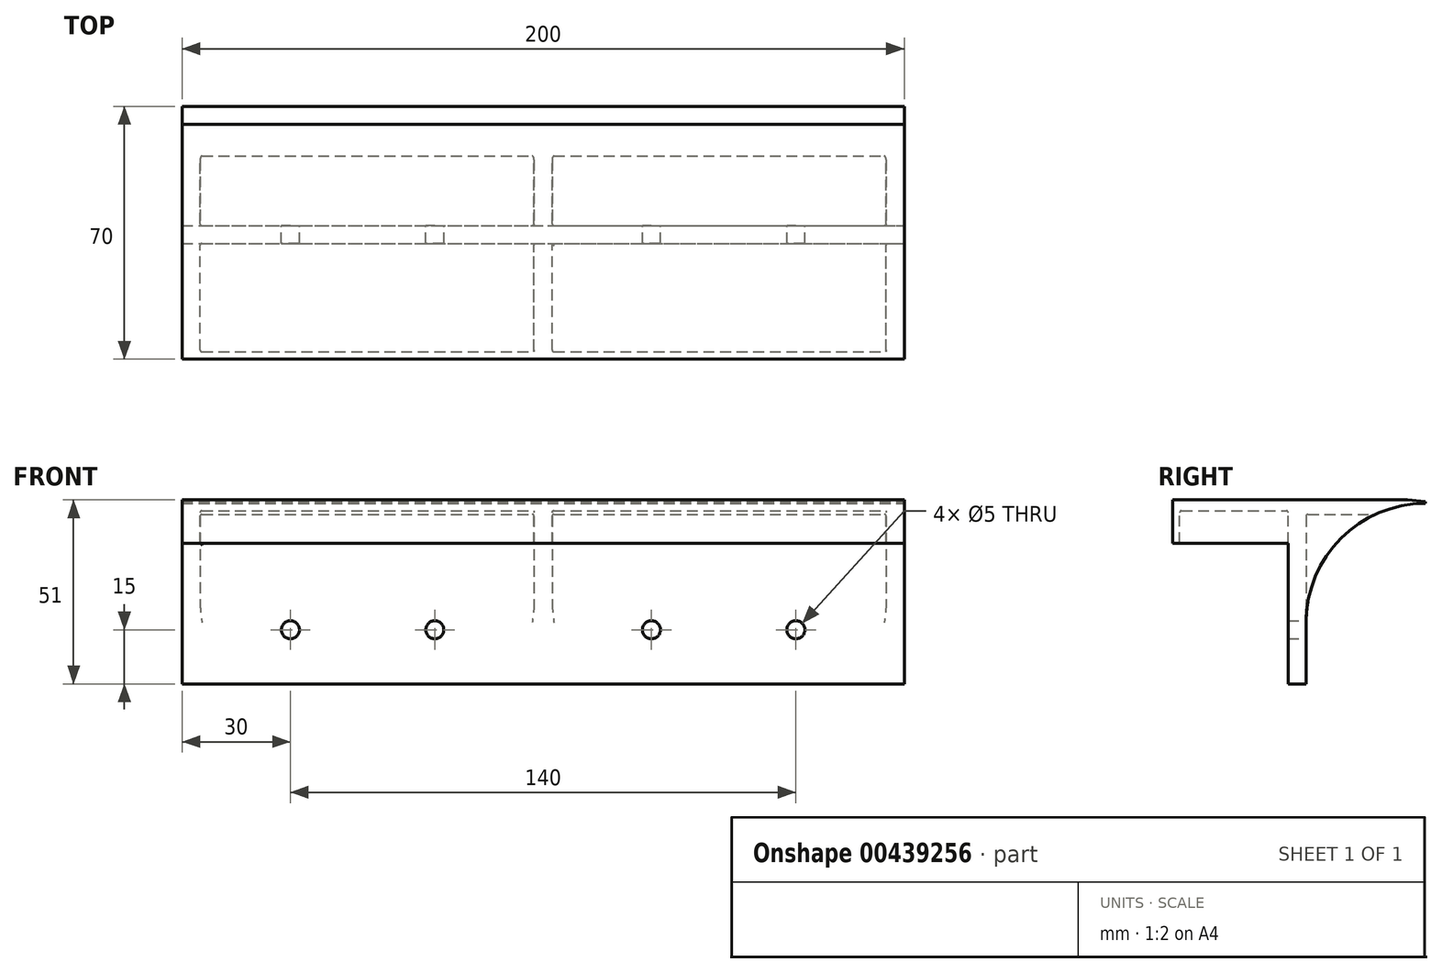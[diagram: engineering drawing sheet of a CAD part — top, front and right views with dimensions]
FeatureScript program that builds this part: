
annotation { "Feature Type Name" : "Feature", "Feature Type Description" : "" }
export const myFeature = defineFeature(function(context is Context, id is Id, definition is map)
    precondition{}
    {
        {
            var Q0;
            Q0=qCreatedBy(makeId("Front.planeOp"),FACE);
            var sketch = newSketch(context, id + "F0", { "sketchPlane" : qUnion([Q0])});
            skLineSegment(sketch, "E0.bottom", {"start": v(0, 0) * mm, "end": v(-200, 0) * mm});
            skLineSegment(sketch, "E0.top", {"start": v(0, -50) * mm, "end": v(-200, -50) * mm});
            skLineSegment(sketch, "E0.left", {"start": v(0, 0) * mm, "end": v(0, -50) * mm});
            skLineSegment(sketch, "E0.right", {"start": v(-200, 0) * mm, "end": v(-200, -50) * mm});
            skLineSegment(sketch, "E1.top", {"start": v(0, 1) * mm, "end": v(-200, 1) * mm});
            skLineSegment(sketch, "E1.left", {"start": v(0, 0) * mm, "end": v(0, 1) * mm});
            skLineSegment(sketch, "E1.right", {"start": v(-200, 0) * mm, "end": v(-200, 1) * mm});
            skSolve(sketch);
        }
        {
            var Q0;
            Q0 = qSketchRegion(id + "F0", true);
            extrude(context, id + "F1", {"entities" : qUnion([Q0]), "depth" : 70 * mm});
        }
        {
            var Q0;
            Q0=qCreatedBy(makeId("Right.planeOp"),FACE);
            var sketch = newSketch(context, id + "F2", { "sketchPlane" : qUnion([Q0])});
            skLineSegment(sketch, "E2.right", {"start": v(-70, -11) * mm, "end": v(-70, -50) * mm});
            skLineSegment(sketch, "E3.top", {"start": v(-70, -11) * mm, "end": v(-38, -11) * mm});
            skLineSegment(sketch, "E3.left", {"start": v(-70, -50) * mm, "end": v(-70, -11) * mm});
            skLineSegment(sketch, "E3.right", {"start": v(-38, -50) * mm, "end": v(-38, -11) * mm});
            skLineSegment(sketch, "E4", {"start": v(-70, -50) * mm, "end": v(-38, -50) * mm});
            skSolve(sketch);
        }
        {
            var Q0;
            Q0 = qSketchRegion(id + "F2", true);
            extrude(context, id + "F3", {"entities" : qUnion([Q0]), "operationType" : NewBodyOperationType.REMOVE, "oppositeDirection" : true, "depth" : 200 * mm});
        }
        {
            var Q0;
            Q0=qCreatedBy(makeId("Right.planeOp"),FACE);
            var sketch = newSketch(context, id + "F4", { "sketchPlane" : qUnion([Q0])});
            skArc(sketch, "E5", {"start": v(0, 0) * mm, "mid": v(-23.33, -9.67) * mm, "end": v(-33, -33) * mm});
            skLineSegment(sketch, "E6", {"start": v(-33, -33) * mm, "end": v(-33, -50) * mm});
            skLineSegment(sketch, "E7", {"start": v(-33, -50) * mm, "end": v(0, -50) * mm});
            skLineSegment(sketch, "E8", {"start": v(0, -50) * mm, "end": v(0, 0) * mm});
            skSolve(sketch);
        }
        {
            var Q0;
            Q0 = qSketchRegion(id + "F4", true);
            extrude(context, id + "F5", {"entities" : qUnion([Q0]), "operationType" : NewBodyOperationType.REMOVE, "oppositeDirection" : true, "depth" : 200 * mm});
        }
        {
            var Q0;
            Q0=qCreatedBy(makeId("Right.planeOp"),FACE);
            var sketch = newSketch(context, id + "F6", { "sketchPlane" : qUnion([Q0])});
            skLineSegment(sketch, "E9.bottom", {"start": v(-68, -11) * mm, "end": v(-38, -11) * mm});
            skLineSegment(sketch, "E9.top", {"start": v(-68, -2) * mm, "end": v(-38, -2) * mm});
            skLineSegment(sketch, "E9.left", {"start": v(-68, -11) * mm, "end": v(-68, -2) * mm});
            skLineSegment(sketch, "E9.right", {"start": v(-38, -11) * mm, "end": v(-38, -2) * mm});
            skSolve(sketch);
        }
        {
            var Q0;
            Q0 = qSketchRegion(id + "F6", true);
            extrude(context, id + "F7", {"entities" : qUnion([Q0]), "operationType" : NewBodyOperationType.REMOVE, "oppositeDirection" : true, "depth" : 195 * mm});
        }
        {
            var Q0;
            Q0 = qSketchRegion(id + "F6", true);
            extrude(context, id + "F8", {"entities" : qUnion([Q0]), "operationType" : NewBodyOperationType.ADD, "oppositeDirection" : true, "depth" : 5 * mm});
        }
        {
            var Q0;
            Q0 = qSketchRegion(id + "F6", true);
            extrude(context, id + "F9", {"entities" : qUnion([Q0]), "operationType" : NewBodyOperationType.ADD, "oppositeDirection" : true, "depth" : 102.5 * mm, "hasSecondDirection" : true, "secondDirectionOppositeDirection" : true, "secondDirectionDepth" : 97.5 * mm});
        }
        {
            var Q0;
            Q0=qCreatedBy(makeId("Right.planeOp"),FACE);
            var sketch = newSketch(context, id + "F10", { "sketchPlane" : qUnion([Q0])});
            skLineSegment(sketch, "E10.bottom", {"start": v(-33, -3) * mm, "end": v(-4.94, -3) * mm});
            skLineSegment(sketch, "E10.top", {"start": v(-33, -33) * mm, "end": v(-4.94, -33) * mm});
            skLineSegment(sketch, "E10.left", {"start": v(-33, -3) * mm, "end": v(-33, -33) * mm});
            skLineSegment(sketch, "E10.right", {"start": v(-4.94, -3) * mm, "end": v(-4.94, -33) * mm});
            skSolve(sketch);
        }
        {
            var Q0;
            Q0 = qSketchRegion(id + "F10", true);
            extrude(context, id + "F11", {"entities" : qUnion([Q0]), "operationType" : NewBodyOperationType.REMOVE, "oppositeDirection" : true, "depth" : 97.5 * mm, "hasSecondDirection" : true, "secondDirectionOppositeDirection" : true, "secondDirectionDepth" : 5 * mm});
        }
        {
            var Q0;
            Q0 = qSketchRegion(id + "F10", true);
            extrude(context, id + "F12", {"entities" : qUnion([Q0]), "operationType" : NewBodyOperationType.REMOVE, "oppositeDirection" : true, "depth" : 195 * mm, "hasSecondDirection" : true, "secondDirectionOppositeDirection" : true, "secondDirectionDepth" : 102.5 * mm});
        }
        {
            var Q0;
            Q0=qCreatedBy(makeId("Front.planeOp"),FACE);
            var sketch = newSketch(context, id + "F13", { "sketchPlane" : qUnion([Q0])});
            skCircle(sketch, "E11", {"center": v(-30, -35) * mm, "radius": 2.5 * mm});
            skCircle(sketch, "E12", {"center": v(-70, -35) * mm, "radius": 2.5 * mm});
            skCircle(sketch, "E13", {"center": v(-130, -35) * mm, "radius": 2.5 * mm});
            skCircle(sketch, "E14", {"center": v(-170, -35) * mm, "radius": 2.5 * mm});
            skSolve(sketch);
        }
        {
            var Q0;
            Q0 = qSketchRegion(id + "F13", true);
            extrude(context, id + "F14", {"entities" : qUnion([Q0]), "operationType" : NewBodyOperationType.REMOVE, "depth" : 60 * mm});
        }
        {
            var Q0;
            Q0=makeQuery(id+"F12.boolean.opBoolean","COPY",EDGE,{"derivedFrom":makeQuery(id+"F12.opExtrude","CAP_EDGE",EDGE,{"disambiguationData":[OSD([sQuery(id+"F10.wireOp",EDGE,"E10.bottom")])],"isStart":false})});
            var Q1;
            Q1=makeQuery(id+"F12.boolean.opBoolean","COPY",EDGE,{"derivedFrom":makeQuery(id+"F12.opExtrude","SWEPT_EDGE",EDGE,{"disambiguationData":[OSD([sQuery(id+"F10.wireOp",EDGE,"E10.bottom"),sQuery(id+"F10.wireOp",EDGE,"E10.left")])]})});
            var Q2;
            Q2=makeQuery(id+"F12.boolean.opBoolean","COPY",EDGE,{"derivedFrom":makeQuery(id+"F12.opExtrude","CAP_EDGE",EDGE,{"disambiguationData":[OSD([sQuery(id+"F10.wireOp",EDGE,"E10.left")])],"isStart":false})});
            var Q3;
            Q3=makeQuery(id+"F11.boolean.opBoolean","COPY",EDGE,{"derivedFrom":makeQuery(id+"F11.opExtrude","CAP_EDGE",EDGE,{"disambiguationData":[OSD([sQuery(id+"F10.wireOp",EDGE,"E10.bottom")])],"isStart":false})});
            var Q4;
            Q4=makeQuery(id+"F11.boolean.opBoolean","COPY",EDGE,{"derivedFrom":makeQuery(id+"F11.opExtrude","CAP_EDGE",EDGE,{"disambiguationData":[OSD([sQuery(id+"F10.wireOp",EDGE,"E10.left")])],"isStart":false})});
            var Q5;
            Q5=makeQuery(id+"F11.boolean.opBoolean","COPY",EDGE,{"derivedFrom":makeQuery(id+"F11.opExtrude","SWEPT_EDGE",EDGE,{"disambiguationData":[OSD([sQuery(id+"F10.wireOp",EDGE,"E10.bottom"),sQuery(id+"F10.wireOp",EDGE,"E10.left")])]})});
            var Q6;
            Q6=makeQuery(id+"F12.boolean.opBoolean","COPY",EDGE,{"derivedFrom":makeQuery(id+"F12.opExtrude","CAP_EDGE",EDGE,{"disambiguationData":[OSD([sQuery(id+"F10.wireOp",EDGE,"E10.left")])],"isStart":true})});
            var Q7;
            Q7=makeQuery(id+"F12.boolean.opBoolean","COPY",EDGE,{"derivedFrom":makeQuery(id+"F12.opExtrude","CAP_EDGE",EDGE,{"disambiguationData":[OSD([sQuery(id+"F10.wireOp",EDGE,"E10.bottom")])],"isStart":true})});
            var Q8;
            Q8=makeQuery(id+"F11.boolean.opBoolean","COPY",EDGE,{"derivedFrom":makeQuery(id+"F11.opExtrude","CAP_EDGE",EDGE,{"disambiguationData":[OSD([sQuery(id+"F10.wireOp",EDGE,"E10.bottom")])],"isStart":true})});
            var Q9;
            Q9=makeQuery(id+"F11.boolean.opBoolean","COPY",EDGE,{"derivedFrom":makeQuery(id+"F11.opExtrude","CAP_EDGE",EDGE,{"disambiguationData":[OSD([sQuery(id+"F10.wireOp",EDGE,"E10.left")])],"isStart":true})});
            var Q10;
            Q10=makeQuery(id+"F9.opExtrude","CAP_EDGE",EDGE,{"disambiguationData":[OSD([sQuery(id+"F6.wireOp",EDGE,"E9.top")])],"isStart":true});
            var Q11;
            {var subQ0=sQuery(id+"F6.wireOp",EDGE,"E9.top");var subQ1=sQuery(id+"F6.wireOp",EDGE,"E9.right");var subQ2=sQuery(id+"F6.wireOp",EDGE,"E9.left");var subQ3=sQuery(id+"F6.wireOp",EDGE,"E9.bottom");Q11=makeQuery(id+"F9.boolean.opBoolean","SPLIT",EDGE,{"disambiguationData":[TD([makeQuery(id+"F8.opExtrude","CAP_FACE",FACE,{"disambiguationData":[OSD([subQ3,subQ0,subQ2,subQ1])],"isStart":false})])],"derivedFrom":makeQuery(id+"F7.boolean.opBoolean","COPY",EDGE,{"derivedFrom":makeQuery(id+"F7.opExtrude","SWEPT_EDGE",EDGE,{"disambiguationData":[OSD([subQ0,subQ1])]})})});}
            var Q12;
            Q12=makeQuery(id+"F7.boolean.opBoolean","COPY",EDGE,{"derivedFrom":makeQuery(id+"F7.opExtrude","CAP_EDGE",EDGE,{"disambiguationData":[OSD([sQuery(id+"F6.wireOp",EDGE,"E9.top")])],"isStart":false})});
            var Q13;
            {var subQ0=sQuery(id+"F6.wireOp",EDGE,"E9.top");var subQ1=sQuery(id+"F6.wireOp",EDGE,"E9.right");var subQ2=sQuery(id+"F6.wireOp",EDGE,"E9.left");var subQ3=sQuery(id+"F6.wireOp",EDGE,"E9.bottom");Q13=makeQuery(id+"F9.boolean.opBoolean","SPLIT",EDGE,{"disambiguationData":[TD([makeQuery(id+"F7.boolean.opBoolean","COPY",FACE,{"derivedFrom":makeQuery(id+"F7.opExtrude","CAP_FACE",FACE,{"disambiguationData":[OSD([subQ3,subQ0,subQ2,subQ1])],"isStart":false})})])],"derivedFrom":makeQuery(id+"F7.boolean.opBoolean","COPY",EDGE,{"derivedFrom":makeQuery(id+"F7.opExtrude","SWEPT_EDGE",EDGE,{"disambiguationData":[OSD([subQ0,subQ1])]})})});}
            var Q14;
            {var subQ0=sQuery(id+"F6.wireOp",EDGE,"E9.right");var subQ1=sQuery(id+"F6.wireOp",EDGE,"E9.left");var subQ2=sQuery(id+"F6.wireOp",EDGE,"E9.top");var subQ3=sQuery(id+"F6.wireOp",EDGE,"E9.bottom");Q14=makeQuery(id+"F9.boolean.opBoolean","SPLIT",EDGE,{"disambiguationData":[TD([makeQuery(id+"F7.boolean.opBoolean","COPY",FACE,{"derivedFrom":makeQuery(id+"F7.opExtrude","CAP_FACE",FACE,{"disambiguationData":[OSD([subQ3,subQ2,subQ1,subQ0])],"isStart":false})})])],"derivedFrom":makeQuery(id+"F7.boolean.opBoolean","COPY",EDGE,{"derivedFrom":makeQuery(id+"F7.opExtrude","SWEPT_EDGE",EDGE,{"disambiguationData":[OSD([subQ2,subQ1])]})})});}
            var Q15;
            Q15=makeQuery(id+"F9.opExtrude","CAP_EDGE",EDGE,{"disambiguationData":[OSD([sQuery(id+"F6.wireOp",EDGE,"E9.top")])],"isStart":false});
            var Q16;
            Q16=makeQuery(id+"F9.opExtrude","CAP_EDGE",EDGE,{"disambiguationData":[OSD([sQuery(id+"F6.wireOp",EDGE,"E9.left")])],"isStart":false});
            var Q17;
            Q17=makeQuery(id+"F7.boolean.opBoolean","COPY",EDGE,{"derivedFrom":makeQuery(id+"F7.opExtrude","CAP_EDGE",EDGE,{"disambiguationData":[OSD([sQuery(id+"F6.wireOp",EDGE,"E9.left")])],"isStart":false})});
            var Q18;
            Q18=makeQuery(id+"F9.opExtrude","CAP_EDGE",EDGE,{"disambiguationData":[OSD([sQuery(id+"F6.wireOp",EDGE,"E9.left")])],"isStart":true});
            var Q19;
            Q19=makeQuery(id+"F8.opExtrude","CAP_EDGE",EDGE,{"disambiguationData":[OSD([sQuery(id+"F6.wireOp",EDGE,"E9.left")])],"isStart":false});
            var Q20;
            Q20=makeQuery(id+"F8.opExtrude","CAP_EDGE",EDGE,{"disambiguationData":[OSD([sQuery(id+"F6.wireOp",EDGE,"E9.top")])],"isStart":false});
            var Q21;
            {var subQ0=sQuery(id+"F6.wireOp",EDGE,"E9.top");var subQ1=sQuery(id+"F6.wireOp",EDGE,"E9.left");var subQ2=sQuery(id+"F6.wireOp",EDGE,"E9.right");var subQ3=sQuery(id+"F6.wireOp",EDGE,"E9.bottom");Q21=makeQuery(id+"F9.boolean.opBoolean","SPLIT",EDGE,{"disambiguationData":[TD([makeQuery(id+"F8.opExtrude","CAP_FACE",FACE,{"disambiguationData":[OSD([subQ3,subQ0,subQ1,subQ2])],"isStart":false})])],"derivedFrom":makeQuery(id+"F7.boolean.opBoolean","COPY",EDGE,{"derivedFrom":makeQuery(id+"F7.opExtrude","SWEPT_EDGE",EDGE,{"disambiguationData":[OSD([subQ0,subQ1])]})})});}
            var Q22;
            Q22=makeQuery(id+"F8.opExtrude","CAP_EDGE",EDGE,{"disambiguationData":[OSD([sQuery(id+"F6.wireOp",EDGE,"E9.right")])],"isStart":false});
            var Q23;
            Q23=makeQuery(id+"F8.opExtrude","SWEPT_EDGE",EDGE,{"disambiguationData":[OSD([sQuery(id+"F6.wireOp",EDGE,"E9.bottom"),sQuery(id+"F6.wireOp",EDGE,"E9.right")])]});
            var Q24;
            Q24=makeQuery(id+"F9.opExtrude","CAP_EDGE",EDGE,{"disambiguationData":[OSD([sQuery(id+"F6.wireOp",EDGE,"E9.right")])],"isStart":false});
            var Q25;
            Q25=makeQuery(id+"F9.opExtrude","SWEPT_EDGE",EDGE,{"disambiguationData":[OSD([sQuery(id+"F6.wireOp",EDGE,"E9.bottom"),sQuery(id+"F6.wireOp",EDGE,"E9.right")])]});
            var Q26;
            Q26=makeQuery(id+"F3.boolean.opBoolean","COPY",EDGE,{"derivedFrom":makeQuery(id+"F3.opExtrude","SWEPT_EDGE",EDGE,{"disambiguationData":[OSD([sQuery(id+"F2.wireOp",EDGE,"E3.top"),sQuery(id+"F2.wireOp",EDGE,"E3.right")])]})});
            var Q27;
            Q27=makeQuery(id+"F7.boolean.opBoolean","COPY",EDGE,{"derivedFrom":makeQuery(id+"F7.opExtrude","CAP_EDGE",EDGE,{"disambiguationData":[OSD([sQuery(id+"F6.wireOp",EDGE,"E9.right")])],"isStart":false})});
            var Q28;
            Q28=makeQuery(id+"F9.opExtrude","CAP_EDGE",EDGE,{"disambiguationData":[OSD([sQuery(id+"F6.wireOp",EDGE,"E9.right")])],"isStart":true});
            fillet(context, id + "F15", {"entities" : qUnion([Q0, Q1, Q2, Q3, Q4, Q5, Q6, Q7, Q8, Q9, Q10, Q11, Q12, Q13, Q14, Q15, Q16, Q17, Q18, Q19, Q20, Q21, Q22, Q23, Q24, Q25, Q26, Q27, Q28]), "radius" : 0.5 * mm, "tangentPropagation" : true, "allowEdgeOverflow" : false});
        }
        {
            var Q0;
            Q0=makeQuery(id+"F1.opExtrude","CAP_EDGE",EDGE,{"disambiguationData":[OSD([sQuery(id+"F0.wireOp",EDGE,"E1.top")])],"isStart":true});
            chamfer(context, id + "F16", {"entities" : qUnion([Q0]), "chamferType" : ChamferType.TWO_OFFSETS, "width1" : 5 * mm, "oppositeDirection" : false, "width2" : 0.5 * mm, "tangentPropagation" : true});
        }
    });
